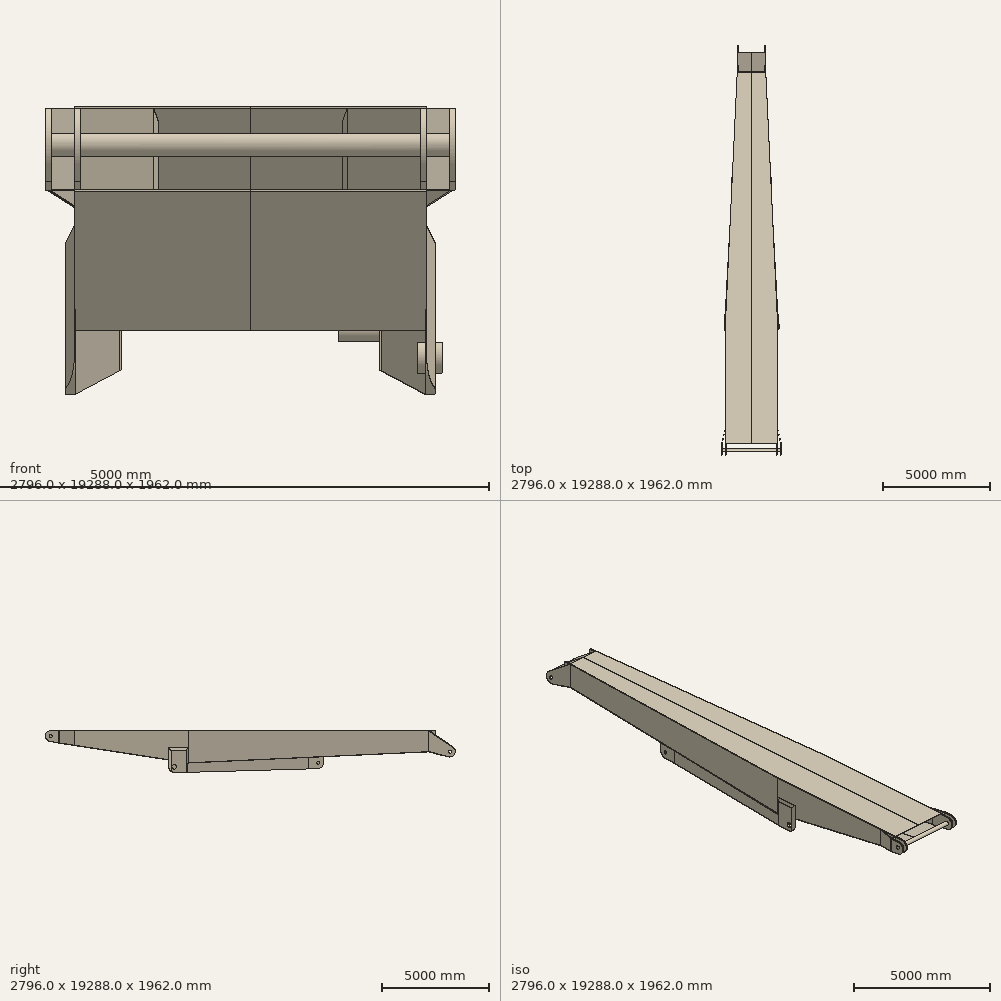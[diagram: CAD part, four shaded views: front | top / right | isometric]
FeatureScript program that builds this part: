
annotation { "Feature Type Name" : "Feature", "Feature Type Description" : "" }
export const myFeature = defineFeature(function(context is Context, id is Id, definition is map)
    precondition{}
    {
        {
            var Q0;
            Q0=qCreatedBy(makeId("Right.planeOp"),FACE);
            cPlane(context, id + "F0", {"entities" : qUnion([Q0]), "cplaneType" : CPlaneType.OFFSET, "offset" : (2384 / 2) * mm, "width" : 150 * mm, "height" : 150 * mm});
        }
        {
            var Q0;
            Q0=qCreatedBy(id+"F0.planeOp",FACE);
            var sketch = newSketch(context, id + "F1", { "sketchPlane" : qUnion([Q0])});
            skCircle(sketch, "E0", {"center": v(0, 0) * mm, "radius": 250 * mm});
            skLineSegment(sketch, "E1", {"start": v(0, 0) * mm, "end": v(5800, 0) * mm, "construction": true});
            skLineSegment(sketch, "E2", {"start": v(5800, 0) * mm, "end": v(5800, -1450) * mm, "construction": true});
            skCircle(sketch, "E3", {"center": v(5800, -1450) * mm, "radius": 250 * mm});
            skLineSegment(sketch, "E4", {"start": v(0, 250) * mm, "end": v(6480, 250) * mm});
            skLineSegment(sketch, "E5", {"start": v(6480, 250) * mm, "end": v(6480, -1250) * mm});
            skLineSegment(sketch, "E6", {"start": v(6480, -1250) * mm, "end": v(-38.02, -247.1) * mm});
            skLineSegment(sketch, "E7", {"start": v(5550, -1450) * mm, "end": v(5550, -1106.9) * mm});
            skLineSegment(sketch, "E8", {"start": v(6480, -1250) * mm, "end": v(5950.6, -1649.55) * mm});
            skCircle(sketch, "E9", {"center": v(0, 0) * mm, "radius": 80 * mm});
            skCircle(sketch, "E10", {"center": v(5800, -1450) * mm, "radius": 105 * mm});
            skLineSegment(sketch, "E11", {"start": v(5550, -1106.9) * mm, "end": v(5550, -550) * mm});
            skLineSegment(sketch, "E12", {"start": v(5550, -550) * mm, "end": v(6480, -550) * mm});
            skLineSegment(sketch, "E13", {"start": v(1050, -414.5) * mm, "end": v(1050, 250) * mm});
            skLineSegment(sketch, "E14", {"start": v(750, -368.34) * mm, "end": v(750, 250) * mm});
            skLineSegment(sketch, "E15", {"start": v(352, -307.1) * mm, "end": v(352, 250) * mm});
            skLineSegment(sketch, "E16", {"start": v(3750, 250) * mm, "end": v(3750, -829.94) * mm});
            skLineSegment(sketch, "E17", {"start": v(5520, 250) * mm, "end": v(5520, -1102.29) * mm});
            skLineSegment(sketch, "E18", {"start": v(6450, 250) * mm, "end": v(6450, -2449.1) * mm});
            skLineSegment(sketch, "E19.1.0.0", {"start": v(9277, 250) * mm, "end": v(9277, -2449.1) * mm});
            skLineSegment(sketch, "E19.2.0.0", {"start": v(12104, 250) * mm, "end": v(12104, -2449.1) * mm});
            skLineSegment(sketch, "E19.direction1", {"start": v(9277, -2449.1) * mm, "end": v(6450, -2449.1) * mm, "construction": true});
            skLineSegment(sketch, "E20.0.3.0", {"start": v(14931, 250) * mm, "end": v(14931, -2449.1) * mm});
            skLineSegment(sketch, "E20.0.4.0", {"start": v(17758, 250) * mm, "end": v(17758, -2449.1) * mm});
            skLineSegment(sketch, "E21", {"start": v(6480, -1250) * mm, "end": v(6480, -2099.61) * mm});
            skLineSegment(sketch, "E22", {"start": v(5800, -1700) * mm, "end": v(6480, -1700) * mm});
            skSolve(sketch);
        }
        {
            var Q0;
            Q0=makeQuery(id+"F9OwMfTJPvjxnqe_1.opExtrude","CAP_FACE",FACE,{"disambiguationData":[OSD([sQuery(id+"F1.wireOp",EDGE,"E0"),sQuery(id+"F1.wireOp",EDGE,"E9")])],"isStart":false});
            var Q1;
            {var subQ5=sQuery(id+"F1.wireOp",EDGE,"E15");Q1=makeQuery(id+"F1.imprint","IMPRINT",FACE,{"disambiguationData":[TD([[makeQuery(id+"F1.imprint","IMPRINT",EDGE,{"derivedFrom":subQ5}),1.0]])]});}
            var Q2;
            Q2=makeQuery(id+"F1.imprint","IMPRINT",FACE,{"disambiguationData":[TD([[makeQuery(id+"F1.imprint","IMPRINT",EDGE,{"derivedFrom":sQuery(id+"F1.wireOp",EDGE,"E9")}),-1.0]])]});
            extrude(context, id + "F2", {"entities" : qUnion([Q0, Q1, Q2]), "depth" : 40 * mm});
        }
        {
            var Q0;
            Q0=makeQuery(id+"F2.opExtrude","SWEPT_BODY",BODY,{"disambiguationData":[OSD([sQuery(id+"F1.wireOp",EDGE,"E0"),sQuery(id+"F1.wireOp",EDGE,"E4"),sQuery(id+"F1.wireOp",EDGE,"E6"),sQuery(id+"F1.wireOp",EDGE,"E9"),sQuery(id+"F1.wireOp",EDGE,"E14")])]});
            var Q1;
            Q1=qCreatedBy(makeId("Right.planeOp"),FACE);
            transform(context, id + "F3", {"entities" : qUnion([Q0]), "transformType" : TransformType.TRANSLATION_DISTANCE, "transformDirection" : qUnion([Q1]), "distance" : (176 - 10) * mm, "makeCopy" : false});
        }
        {
            var Q0;
            {var subQ0=sQuery(id+"F1.wireOp",EDGE,"E7");Q0=makeQuery(id+"F1.imprint","IMPRINT",FACE,{"disambiguationData":[TD([[makeQuery(id+"F1.imprint","IMPRINT",EDGE,{"derivedFrom":subQ0}),-1.0]])]});}
            var Q1;
            Q1=makeQuery(id+"F1.imprint","IMPRINT",FACE,{"disambiguationData":[TD([[makeQuery(id+"F1.imprint","IMPRINT",EDGE,{"derivedFrom":sQuery(id+"F1.wireOp",EDGE,"E10")}),-1.0]])]});
            var Q2;
            {var subQ4=sQuery(id+"F1.wireOp",EDGE,"E11");Q2=makeQuery(id+"F1.imprint","IMPRINT",FACE,{"disambiguationData":[TD([[makeQuery(id+"F1.imprint","IMPRINT",EDGE,{"derivedFrom":subQ4}),-1.0]])]});}
            var Q3;
            {var subQ1=sQuery(id+"F1.wireOp",EDGE,"E5");var subQ3=sQuery(id+"F1.wireOp",EDGE,"E12");var subQ4=makeQuery(id+"F1.imprint","INTERSECT",VERTEX,{"derivedFrom":[subQ1,subQ3]});Q3=makeQuery(id+"F1.imprint","IMPRINT",FACE,{"disambiguationData":[TD([[makeQuery(id+"F1.imprint","IMPRINT",EDGE,{"disambiguationData":[TD([[subQ4,1.0]])],"derivedFrom":subQ3}),-1.0]])]});}
            var Q4;
            {var subQ0=sQuery(id+"F1.wireOp",EDGE,"E8");var subQ3=sQuery(id+"F1.wireOp",EDGE,"E18");var subQ5=makeQuery(id+"F1.imprint","INTERSECT",VERTEX,{"derivedFrom":[subQ0,subQ3]});Q4=makeQuery(id+"F1.imprint","IMPRINT",FACE,{"disambiguationData":[TD([[makeQuery(id+"F1.imprint","IMPRINT",EDGE,{"disambiguationData":[TD([[subQ5,1.0]])],"derivedFrom":subQ3}),1.0]])]});}
            var Q5;
            {var subQ0=sQuery(id+"F1.wireOp",EDGE,"E8");var subQ1=sQuery(id+"F1.wireOp",EDGE,"E3");var subQ2=makeQuery(id+"F1.imprint","INTERSECT",VERTEX,{"derivedFrom":[subQ1,subQ0]});Q5=makeQuery(id+"F1.imprint","IMPRINT",FACE,{"disambiguationData":[TD([[makeQuery(id+"F1.imprint","IMPRINT",EDGE,{"disambiguationData":[TD([[subQ2,1.0]])],"derivedFrom":subQ1}),-1.0]])]});}
            var Q6;
            {var subQ3=sQuery(id+"F1.wireOp",EDGE,"E18");var subQ5=sQuery(id+"F1.wireOp",EDGE,"E22");var subQ7=makeQuery(id+"F1.imprint","INTERSECT",VERTEX,{"derivedFrom":[subQ3,subQ5]});Q6=makeQuery(id+"F1.imprint","IMPRINT",FACE,{"disambiguationData":[TD([[makeQuery(id+"F1.imprint","IMPRINT",EDGE,{"disambiguationData":[TD([[subQ7,1.0]])],"derivedFrom":subQ3}),1.0]])]});}
            extrude(context, id + "F4", {"entities" : qUnion([Q0, Q1, Q2, Q3, Q4, Q5, Q6]), "depth" : 70 * mm});
        }
        {
            var Q0;
            Q0=makeQuery(id+"F4.opExtrude","CAP_EDGE",EDGE,{"disambiguationData":[OSD([sQuery(id+"F1.wireOp",EDGE,"E7"),sQuery(id+"F1.wireOp",EDGE,"E11")])],"isStart":false});
            var Q1;
            Q1=makeQuery(id+"F4.opExtrude","CAP_EDGE",EDGE,{"disambiguationData":[OSD([sQuery(id+"F1.wireOp",EDGE,"E5")])],"isStart":false});
            var Q2;
            Q2=makeQuery(id+"F4.opExtrude","CAP_EDGE",EDGE,{"disambiguationData":[OSD([sQuery(id+"F1.wireOp",EDGE,"E12")])],"isStart":false});
            chamfer(context, id + "F5", {"entities" : qUnion([Q0, Q1, Q2]), "chamferType" : ChamferType.TWO_OFFSETS, "width1" : 60 * mm, "oppositeDirection" : false, "width2" : 120 * mm});
        }
        {
            var Q0;
            {var subQ0=sQuery(id+"F1.wireOp",EDGE,"E11");Q0=makeQuery(id+"F1.imprint","IMPRINT",FACE,{"disambiguationData":[TD([[makeQuery(id+"F1.imprint","IMPRINT",EDGE,{"derivedFrom":subQ0}),1.0]])]});}
            var Q1;
            {var subQ0=sQuery(id+"F1.wireOp",EDGE,"E13");Q1=makeQuery(id+"F1.imprint","IMPRINT",FACE,{"disambiguationData":[TD([[makeQuery(id+"F1.imprint","IMPRINT",EDGE,{"derivedFrom":subQ0}),1.0]])]});}
            var Q2;
            {var subQ0=sQuery(id+"F1.wireOp",EDGE,"E16");Q2=makeQuery(id+"F1.imprint","IMPRINT",FACE,{"disambiguationData":[TD([[makeQuery(id+"F1.imprint","IMPRINT",EDGE,{"derivedFrom":subQ0}),1.0]])]});}
            var Q3;
            {var subQ0=sQuery(id+"F1.wireOp",EDGE,"E13");Q3=makeQuery(id+"F1.imprint","IMPRINT",FACE,{"disambiguationData":[TD([[makeQuery(id+"F1.imprint","IMPRINT",EDGE,{"derivedFrom":subQ0}),-1.0]])]});}
            var Q4;
            {var subQ0=sQuery(id+"F1.wireOp",EDGE,"E5");var subQ1=sQuery(id+"F1.wireOp",EDGE,"E4");var subQ2=makeQuery(id+"F1.imprint","INTERSECT",VERTEX,{"derivedFrom":[subQ1,subQ0]});Q4=makeQuery(id+"F1.imprint","IMPRINT",FACE,{"disambiguationData":[TD([[makeQuery(id+"F1.imprint","IMPRINT",EDGE,{"disambiguationData":[TD([[subQ2,1.0]])],"derivedFrom":subQ1}),-1.0]])]});}
            extrude(context, id + "F6", {"entities" : qUnion([Q0, Q1, Q2, Q3, Q4]), "depth" : 10 * mm});
        }
        {
            var Q0;
            Q0=makeQuery(id+"F1.imprint","IMPRINT",FACE,{"disambiguationData":[TD([[makeQuery(id+"F1.imprint","IMPRINT",EDGE,{"derivedFrom":sQuery(id+"F1.wireOp",EDGE,"E9")}),-1.0]])]});
            var Q1;
            {var subQ5=sQuery(id+"F1.wireOp",EDGE,"E14");Q1=makeQuery(id+"F1.imprint","IMPRINT",FACE,{"disambiguationData":[TD([[makeQuery(id+"F1.imprint","IMPRINT",EDGE,{"derivedFrom":subQ5}),1.0]])]});}
            var Q2;
            {var subQ5=sQuery(id+"F1.wireOp",EDGE,"E15");Q2=makeQuery(id+"F1.imprint","IMPRINT",FACE,{"disambiguationData":[TD([[makeQuery(id+"F1.imprint","IMPRINT",EDGE,{"derivedFrom":subQ5}),1.0]])]});}
            extrude(context, id + "F7", {"entities" : qUnion([Q0, Q1, Q2]), "oppositeDirection" : true, "depth" : 30 * mm, "hasSecondDirection" : true, "secondDirectionOppositeDirection" : false, "secondDirectionDepth" : 10 * mm});
        }
        {
            var Q0;
            Q0=qCreatedBy(makeId("Top.planeOp"),FACE);
            cPlane(context, id + "F8", {"entities" : qUnion([Q0]), "cplaneType" : CPlaneType.OFFSET, "offset" : 250 * mm, "width" : 150 * mm, "height" : 150 * mm});
        }
        {
            var Q0;
            Q0=qCreatedBy(id+"F8.planeOp",FACE);
            var sketch = newSketch(context, id + "F9", { "sketchPlane" : qUnion([Q0])});
            skLineSegment(sketch, "E23", {"start": v(0, 338) * mm, "end": v(1202, 338) * mm});
            skLineSegment(sketch, "E24", {"start": v(1202, 338) * mm, "end": v(1202, 6480) * mm});
            skLineSegment(sketch, "E25", {"start": v(1202, 6480) * mm, "end": v(0, 6480) * mm});
            skLineSegment(sketch, "E26", {"start": v(0, 6480) * mm, "end": v(0, 338) * mm});
            skLineSegment(sketch, "E27", {"start": v(0, 6480) * mm, "end": v(0, 17788) * mm});
            skLineSegment(sketch, "E28", {"start": v(0, 17788) * mm, "end": v(670.76, 17788) * mm});
            skLineSegment(sketch, "E29", {"start": v(1202, 6480) * mm, "end": v(670.76, 17788) * mm});
            skLineSegment(sketch, "E30", {"start": v(1191.99, 6480) * mm, "end": v(660.75, 17788) * mm});
            skPoint(sketch, "E31.0", {"position": v(0, 0) * mm});
            skSolve(sketch);
        }
        {
            var Q0;
            {var subQ0=sQuery(id+"F9.wireOp",EDGE,"E25");Q0=makeQuery(id+"F9.imprint","IMPRINT",FACE,{"disambiguationData":[TD([[makeQuery(id+"F9.imprint","IMPRINT",EDGE,{"derivedFrom":subQ0}),1.0]])]});}
            var Q1;
            Q1=makeQuery(id+"F9.imprint","IMPRINT",FACE,{"disambiguationData":[TD([[makeQuery(id+"F9.imprint","IMPRINT",EDGE,{"derivedFrom":sQuery(id+"F9.wireOp",EDGE,"E25")}),-1.0]])]});
            extrude(context, id + "F10", {"entities" : qUnion([Q0, Q1]), "depth" : 12 * mm});
        }
        {
            var Q0;
            Q0=makeQuery(id+"F2.opExtrude","SWEPT_FACE",FACE,{"disambiguationData":[OSD([sQuery(id+"F1.wireOp",EDGE,"E4")])]});
            var sketch = newSketch(context, id + "F11", { "sketchPlane" : qUnion([Q0])});
            skLineSegment(sketch, "E32.0", {"start": v(1202, 338) * mm, "end": v(1202, 6480) * mm});
            skLineSegment(sketch, "E33", {"start": v(1358, 352) * mm, "end": v(1358, 402) * mm});
            skLineSegment(sketch, "E34", {"start": v(1358, 402) * mm, "end": v(1202, 1050.5) * mm});
            skLineSegment(sketch, "E35.0", {"start": v(1373.43, 402) * mm, "end": v(1202, 1114.64) * mm});
            skLineSegment(sketch, "E36", {"start": v(1373.43, 402) * mm, "end": v(1398, 352) * mm});
            skLineSegment(sketch, "E37", {"start": v(1398, 352) * mm, "end": v(1358, 352) * mm});
            skLineSegment(sketch, "E38", {"start": v(1202, 1114.64) * mm, "end": v(1202, 1050.5) * mm});
            skLineSegment(sketch, "E39.bottom", {"start": v(1358, 352) * mm, "end": v(1202, 352) * mm});
            skLineSegment(sketch, "E39.top", {"start": v(1358, 340) * mm, "end": v(1202, 340) * mm});
            skLineSegment(sketch, "E39.left", {"start": v(1358, 352) * mm, "end": v(1358, 340) * mm});
            skLineSegment(sketch, "E39.right", {"start": v(1202, 352) * mm, "end": v(1202, 340) * mm});
            skSolve(sketch);
        }
        {
            var Q0;
            Q0=makeQuery(id+"F11.imprint","IMPRINT",FACE,{"disambiguationData":[TD([[makeQuery(id+"F11.imprint","IMPRINT",EDGE,{"derivedFrom":sQuery(id+"F11.wireOp",EDGE,"E33")}),-1.0]])]});
            extrude(context, id + "F12", {"entities" : qUnion([Q0]), "oppositeDirection" : true, "depth" : 800 * mm});
        }
        {
            var Q0;
            Q0=makeQuery(id+"F11.imprint","IMPRINT",FACE,{"disambiguationData":[TD([[makeQuery(id+"F11.imprint","IMPRINT",EDGE,{"derivedFrom":sQuery(id+"F11.wireOp",EDGE,"E39.bottom")}),1.0]])]});
            extrude(context, id + "F13", {"entities" : qUnion([Q0]), "oppositeDirection" : true, "depth" : 1000 * mm});
        }
        {
            var Q0;
            Q0=makeQuery(id+"F2.opExtrude","SWEPT_FACE",FACE,{"disambiguationData":[OSD([sQuery(id+"F1.wireOp",EDGE,"E6")])]});
            var sketch = newSketch(context, id + "F14", { "sketchPlane" : qUnion([Q0])});
            skLineSegment(sketch, "E40.bottom", {"start": v(1398, -318.7) * mm, "end": v(966.19, -318.7) * mm});
            skLineSegment(sketch, "E40.top", {"start": v(1398, -1467.1) * mm, "end": v(966.19, -1467.1) * mm});
            skLineSegment(sketch, "E40.left", {"start": v(1398, -318.7) * mm, "end": v(1398, -1467.1) * mm});
            skLineSegment(sketch, "E40.right", {"start": v(966.19, -318.7) * mm, "end": v(966.19, -1467.1) * mm});
            skSolve(sketch);
        }
        {
            var Q0;
            Q0 = qSketchRegion(id + "F14", true);
            extrude(context, id + "F15", {"entities" : qUnion([Q0]), "operationType" : NewBodyOperationType.REMOVE, "depth" : 500 * mm});
        }
        {
            var Q0;
            {var subQ0=sQuery(id+"F9.wireOp",EDGE,"E29");Q0=makeQuery(id+"F9.imprint","IMPRINT",FACE,{"disambiguationData":[TD([[makeQuery(id+"F9.imprint","IMPRINT",EDGE,{"derivedFrom":subQ0}),1.0]])]});}
            extrude(context, id + "F16", {"entities" : qUnion([Q0]), "oppositeDirection" : true, "depth" : 1500 * mm});
        }
        {
            var Q0;
            Q0=qCreatedBy(makeId("Right.planeOp"),FACE);
            var sketch = newSketch(context, id + "F17", { "sketchPlane" : qUnion([Q0])});
            skLineSegment(sketch, "E41.left", {"start": v(6480, -1250) * mm, "end": v(6480, -1250) * mm});
            skLineSegment(sketch, "E42", {"start": v(6480, -1250) * mm, "end": v(17788, -726.7) * mm});
            skLineSegment(sketch, "E43", {"start": v(17788, -726.7) * mm, "end": v(17837.95, -724.39) * mm});
            skLineSegment(sketch, "E44", {"start": v(17837.95, -724.39) * mm, "end": v(17837.95, -1250) * mm});
            skLineSegment(sketch, "E45", {"start": v(17837.95, -1250) * mm, "end": v(17788, -1250) * mm});
            skLineSegment(sketch, "E46.0", {"start": v(6480, -1250) * mm, "end": v(17788, -1250) * mm});
            skSolve(sketch);
        }
        {
            var Q0;
            {var subQ0=sQuery(id+"F17.wireOp",EDGE,"E42");Q0=makeQuery(id+"F17.imprint","IMPRINT",FACE,{"disambiguationData":[TD([[makeQuery(id+"F17.imprint","IMPRINT",EDGE,{"derivedFrom":subQ0}),-1.0]])]});}
            var Q1;
            {var subQ0=sQuery(id+"F17.wireOp",EDGE,"E43");Q1=makeQuery(id+"F17.imprint","IMPRINT",FACE,{"disambiguationData":[TD([[makeQuery(id+"F17.imprint","IMPRINT",EDGE,{"derivedFrom":subQ0}),-1.0]])]});}
            extrude(context, id + "F18", {"entities" : qUnion([Q0, Q1]), "operationType" : NewBodyOperationType.REMOVE, "endBound" : BoundingType.THROUGH_ALL, "depth" : 25 * mm});
        }
        {
            var Q0;
            Q0=makeQuery(id+"F18.boolean.opBoolean","COPY",FACE,{"derivedFrom":makeQuery(id+"F18.opExtrude","SWEPT_FACE",FACE,{"disambiguationData":[OSD([sQuery(id+"F17.wireOp",EDGE,"E42"),sQuery(id+"F17.wireOp",EDGE,"E43")])]})});
            var sketch = newSketch(context, id + "F19", { "sketchPlane" : qUnion([Q0])});
            skLineSegment(sketch, "E47", {"start": v(1202, -6415.29) * mm, "end": v(670.76, -17735.39) * mm});
            skLineSegment(sketch, "E48", {"start": v(670.76, -17735.39) * mm, "end": v(0, -17735.39) * mm});
            skLineSegment(sketch, "E49", {"start": v(1202, -6415.29) * mm, "end": v(0, -6415.29) * mm});
            skLineSegment(sketch, "E50", {"start": v(0, -6415.29) * mm, "end": v(0, -17735.39) * mm});
            skSolve(sketch);
        }
        {
            var Q0;
            Q0=makeQuery(id+"F19.imprint","IMPRINT",FACE,{"disambiguationData":[TD([[makeQuery(id+"F19.imprint","IMPRINT",EDGE,{"derivedFrom":sQuery(id+"F19.wireOp",EDGE,"E48")}),-1.0]])]});
            var Q1;
            {var subQ0=sQuery(id+"F19.wireOp",EDGE,"E47");Q1=makeQuery(id+"F19.imprint","IMPRINT",FACE,{"disambiguationData":[TD([[makeQuery(id+"F19.imprint","IMPRINT",EDGE,{"derivedFrom":subQ0}),-1.0]])]});}
            var Q2;
            Q2=makeQuery(id+"F19.imprint","IMPRINT",FACE,{"disambiguationData":[TD([[makeQuery(id+"F19.imprint","IMPRINT",EDGE,{"derivedFrom":sQuery(id+"F19.wireOp",EDGE,"E49")}),1.0]])]});
            extrude(context, id + "F20", {"entities" : qUnion([Q0, Q1, Q2]), "depth" : 12 * mm});
        }
        {
            var Q0;
            {var subQ0=sQuery(id+"F1.wireOp",EDGE,"E11");Q0=makeQuery(id+"F1.imprint","IMPRINT",FACE,{"disambiguationData":[TD([[makeQuery(id+"F1.imprint","IMPRINT",EDGE,{"derivedFrom":subQ0}),1.0]])]});}
            var sketch = newSketch(context, id + "F21", { "sketchPlane" : qUnion([Q0])});
            skPoint(sketch, "E51.0", {"position": v(750, -368.34) * mm});
            skLineSegment(sketch, "E52", {"start": v(337.17, -304.82) * mm, "end": v(6480, -1250) * mm});
            skLineSegment(sketch, "E53", {"start": v(6480, -1250) * mm, "end": v(6478.18, -1261.86) * mm});
            skLineSegment(sketch, "E54", {"start": v(6480, -1250) * mm, "end": v(6480.55, -1261.99) * mm});
            skLineSegment(sketch, "E55", {"start": v(6480.55, -1261.99) * mm, "end": v(6478.18, -1261.86) * mm});
            skLineSegment(sketch, "E56", {"start": v(6478.18, -1261.86) * mm, "end": v(335.35, -316.68) * mm});
            skLineSegment(sketch, "E57", {"start": v(335.35, -316.68) * mm, "end": v(337.17, -304.82) * mm});
            skLineSegment(sketch, "E58.0", {"start": v(6480.55, -1261.99) * mm, "end": v(6480, -1250) * mm});
            skSolve(sketch);
        }
        {
            var Q0;
            {var subQ0=sQuery(id+"F21.wireOp",EDGE,"E53");Q0=makeQuery(id+"F21.imprint","IMPRINT",FACE,{"disambiguationData":[TD([[makeQuery(id+"F21.imprint","IMPRINT",EDGE,{"derivedFrom":subQ0}),-1.0]])]});}
            var Q1;
            Q1=makeQuery(id+"F21.imprint","IMPRINT",FACE,{"disambiguationData":[TD([[makeQuery(id+"F21.imprint","IMPRINT",EDGE,{"derivedFrom":sQuery(id+"F21.wireOp",EDGE,"E53")}),1.0]])]});
            var Q2;
            Q2=makeQuery(id+"F10.opExtrude","SWEPT_FACE",FACE,{"disambiguationData":[OSD([sQuery(id+"F9.wireOp",EDGE,"E26"),sQuery(id+"F9.wireOp",EDGE,"E27")])]});
            extrude(context, id + "F22", {"entities" : qUnion([Q0, Q1]), "endBound" : BoundingType.UP_TO_SURFACE, "oppositeDirection" : true, "endBoundEntityFace" : qUnion([Q2]), "depth" : 25 * mm, "hasSecondDirection" : true, "secondDirectionOppositeDirection" : false, "secondDirectionDepth" : 10 * mm});
        }
        {
            var Q0;
            Q0=makeQuery(id+"F4.opExtrude","SWEPT_BODY",BODY,{"disambiguationData":[OSD([sQuery(id+"F1.wireOp",EDGE,"E3"),sQuery(id+"F1.wireOp",EDGE,"E5"),sQuery(id+"F1.wireOp",EDGE,"E7"),sQuery(id+"F1.wireOp",EDGE,"E8"),sQuery(id+"F1.wireOp",EDGE,"E10"),sQuery(id+"F1.wireOp",EDGE,"E11"),sQuery(id+"F1.wireOp",EDGE,"E12")])]});
            var Q1;
            Q1=makeQuery(id+"F22.opExtrude","SWEPT_BODY",BODY,{"disambiguationData":[OSD([sQuery(id+"F21.wireOp",EDGE,"E52"),sQuery(id+"F21.wireOp",EDGE,"E53"),sQuery(id+"F21.wireOp",EDGE,"E56"),sQuery(id+"F21.wireOp",EDGE,"E57")])]});
            booleanBodies(context, id + "F23", {"operationType" : BooleanOperationType.SUBTRACTION, "tools" : qUnion([Q0]), "targets" : qUnion([Q1]), "keepTools" : true});
        }
        {
            var Q0;
            Q0=qCreatedBy(id+"F8.planeOp",FACE);
            var sketch = newSketch(context, id + "F24", { "sketchPlane" : qUnion([Q0])});
            skPoint(sketch, "E59.0", {"position": v(1192, 3750) * mm});
            skPoint(sketch, "E60.0", {"position": v(1192, 352) * mm});
            skPoint(sketch, "E61.0", {"position": v(1192, 1050) * mm});
            skPoint(sketch, "E62.0", {"position": v(1192, 5520) * mm});
            skPoint(sketch, "E63.0", {"position": v(1192, 6450) * mm});
            skPoint(sketch, "E64.0", {"position": v(1192, 9277) * mm});
            skPoint(sketch, "E65.0", {"position": v(1192, 12104) * mm});
            skPoint(sketch, "E66.0", {"position": v(1192, 14931) * mm});
            skPoint(sketch, "E67.0", {"position": v(1192, 17758) * mm});
            skLineSegment(sketch, "E68.bottom", {"start": v(1192, 340) * mm, "end": v(0, 340) * mm});
            skLineSegment(sketch, "E68.top", {"start": v(1192, 352) * mm, "end": v(0, 352) * mm});
            skLineSegment(sketch, "E68.left", {"start": v(1192, 340) * mm, "end": v(1192, 352) * mm});
            skLineSegment(sketch, "E68.right", {"start": v(0, 340) * mm, "end": v(0, 352) * mm});
            skPoint(sketch, "E69.0", {"position": v(0, 0) * mm});
            skLineSegment(sketch, "E70", {"start": v(0, 0) * mm, "end": v(0, 18574) * mm, "construction": true});
            skLineSegment(sketch, "E71.bottom", {"start": v(1192, 1050) * mm, "end": v(0, 1050) * mm});
            skLineSegment(sketch, "E71.top", {"start": v(1192, 1062) * mm, "end": v(0, 1062) * mm});
            skLineSegment(sketch, "E71.left", {"start": v(1192, 1050) * mm, "end": v(1192, 1062) * mm});
            skLineSegment(sketch, "E71.right", {"start": v(0, 1050) * mm, "end": v(0, 1062) * mm});
            skLineSegment(sketch, "E72.bottom", {"start": v(1192, 3750) * mm, "end": v(0, 3750) * mm});
            skLineSegment(sketch, "E72.top", {"start": v(1192, 3762) * mm, "end": v(0, 3762) * mm});
            skLineSegment(sketch, "E72.left", {"start": v(1192, 3750) * mm, "end": v(1192, 3762) * mm});
            skLineSegment(sketch, "E72.right", {"start": v(0, 3750) * mm, "end": v(0, 3762) * mm});
            skLineSegment(sketch, "E73.bottom", {"start": v(1192, 5520) * mm, "end": v(0, 5520) * mm});
            skLineSegment(sketch, "E73.top", {"start": v(1192, 5530) * mm, "end": v(0, 5530) * mm});
            skLineSegment(sketch, "E73.left", {"start": v(1192, 5520) * mm, "end": v(1192, 5530) * mm});
            skLineSegment(sketch, "E73.right", {"start": v(0, 5520) * mm, "end": v(0, 5530) * mm});
            skLineSegment(sketch, "E74.bottom", {"start": v(1192, 6450) * mm, "end": v(0, 6450) * mm});
            skLineSegment(sketch, "E74.top", {"start": v(1192, 6460) * mm, "end": v(0, 6460) * mm});
            skLineSegment(sketch, "E74.left", {"start": v(1192, 6450) * mm, "end": v(1192, 6460) * mm});
            skLineSegment(sketch, "E74.right", {"start": v(0, 6450) * mm, "end": v(0, 6460) * mm});
            skLineSegment(sketch, "E75.bottom", {"start": v(1192, 9277) * mm, "end": v(0, 9277) * mm});
            skLineSegment(sketch, "E75.top", {"start": v(1192, 9287) * mm, "end": v(0, 9287) * mm});
            skLineSegment(sketch, "E75.left", {"start": v(1192, 9277) * mm, "end": v(1192, 9287) * mm});
            skLineSegment(sketch, "E75.right", {"start": v(0, 9277) * mm, "end": v(0, 9287) * mm});
            skLineSegment(sketch, "E76.bottom", {"start": v(1192, 12104) * mm, "end": v(0, 12104) * mm});
            skLineSegment(sketch, "E76.top", {"start": v(1192, 12114) * mm, "end": v(0, 12114) * mm});
            skLineSegment(sketch, "E76.left", {"start": v(1192, 12104) * mm, "end": v(1192, 12114) * mm});
            skLineSegment(sketch, "E76.right", {"start": v(0, 12104) * mm, "end": v(0, 12114) * mm});
            skLineSegment(sketch, "E77.bottom", {"start": v(1192, 14931) * mm, "end": v(0, 14931) * mm});
            skLineSegment(sketch, "E77.top", {"start": v(1192, 14941) * mm, "end": v(0, 14941) * mm});
            skLineSegment(sketch, "E77.left", {"start": v(1192, 14931) * mm, "end": v(1192, 14941) * mm});
            skLineSegment(sketch, "E77.right", {"start": v(0, 14931) * mm, "end": v(0, 14941) * mm});
            skLineSegment(sketch, "E78.bottom", {"start": v(1192, 17758) * mm, "end": v(0, 17758) * mm});
            skLineSegment(sketch, "E78.top", {"start": v(1192, 17768) * mm, "end": v(0, 17768) * mm});
            skLineSegment(sketch, "E78.left", {"start": v(1192, 17758) * mm, "end": v(1192, 17768) * mm});
            skLineSegment(sketch, "E78.right", {"start": v(0, 17758) * mm, "end": v(0, 17768) * mm});
            skSolve(sketch);
        }
        {
            var Q0;
            Q0=makeQuery(id+"F24.imprint","IMPRINT",FACE,{"disambiguationData":[TD([[makeQuery(id+"F24.imprint","IMPRINT",EDGE,{"derivedFrom":sQuery(id+"F24.wireOp",EDGE,"E68.bottom")}),-1.0]])]});
            var Q1;
            Q1=makeQuery(id+"F24.imprint","IMPRINT",FACE,{"disambiguationData":[TD([[makeQuery(id+"F24.imprint","IMPRINT",EDGE,{"derivedFrom":sQuery(id+"F24.wireOp",EDGE,"E71.bottom")}),-1.0]])]});
            var Q2;
            Q2=makeQuery(id+"F24.imprint","IMPRINT",FACE,{"disambiguationData":[TD([[makeQuery(id+"F24.imprint","IMPRINT",EDGE,{"derivedFrom":sQuery(id+"F24.wireOp",EDGE,"E72.bottom")}),-1.0]])]});
            var Q3;
            Q3=makeQuery(id+"F24.imprint","IMPRINT",FACE,{"disambiguationData":[TD([[makeQuery(id+"F24.imprint","IMPRINT",EDGE,{"derivedFrom":sQuery(id+"F24.wireOp",EDGE,"E73.bottom")}),-1.0]])]});
            var Q4;
            Q4=makeQuery(id+"F24.imprint","IMPRINT",FACE,{"disambiguationData":[TD([[makeQuery(id+"F24.imprint","IMPRINT",EDGE,{"derivedFrom":sQuery(id+"F24.wireOp",EDGE,"E74.bottom")}),-1.0]])]});
            var Q5;
            Q5=makeQuery(id+"F24.imprint","IMPRINT",FACE,{"disambiguationData":[TD([[makeQuery(id+"F24.imprint","IMPRINT",EDGE,{"derivedFrom":sQuery(id+"F24.wireOp",EDGE,"E75.bottom")}),-1.0]])]});
            var Q6;
            Q6=makeQuery(id+"F24.imprint","IMPRINT",FACE,{"disambiguationData":[TD([[makeQuery(id+"F24.imprint","IMPRINT",EDGE,{"derivedFrom":sQuery(id+"F24.wireOp",EDGE,"E76.bottom")}),-1.0]])]});
            var Q7;
            Q7=makeQuery(id+"F24.imprint","IMPRINT",FACE,{"disambiguationData":[TD([[makeQuery(id+"F24.imprint","IMPRINT",EDGE,{"derivedFrom":sQuery(id+"F24.wireOp",EDGE,"E77.bottom")}),-1.0]])]});
            var Q8;
            Q8=makeQuery(id+"F24.imprint","IMPRINT",FACE,{"disambiguationData":[TD([[makeQuery(id+"F24.imprint","IMPRINT",EDGE,{"derivedFrom":sQuery(id+"F24.wireOp",EDGE,"E78.bottom")}),-1.0]])]});
            extrude(context, id + "F25", {"entities" : qUnion([Q0, Q1, Q2, Q3, Q4, Q5, Q6, Q7, Q8]), "oppositeDirection" : true, "depth" : 2000 * mm});
        }
        {
            var Q0;
            Q0=makeQuery(id+"F22.opExtrude","SWEPT_BODY",BODY,{"disambiguationData":[OSD([sQuery(id+"F21.wireOp",EDGE,"E52"),sQuery(id+"F21.wireOp",EDGE,"E54"),sQuery(id+"F21.wireOp",EDGE,"E55"),sQuery(id+"F21.wireOp",EDGE,"E56"),sQuery(id+"F21.wireOp",EDGE,"E57")])]});
            var Q1;
            Q1=makeQuery(id+"F20.opExtrude","SWEPT_BODY",BODY,{"disambiguationData":[OSD([sQuery(id+"F19.wireOp",EDGE,"E47"),sQuery(id+"F19.wireOp",EDGE,"E48"),sQuery(id+"F19.wireOp",EDGE,"E49"),sQuery(id+"F19.wireOp",EDGE,"E50")])]});
            var Q2;
            Q2=makeQuery(id+"F16.opExtrude","SWEPT_BODY",BODY,{"disambiguationData":[OSD([sQuery(id+"F9.wireOp",EDGE,"E25"),sQuery(id+"F9.wireOp",EDGE,"E28"),sQuery(id+"F9.wireOp",EDGE,"E29"),sQuery(id+"F9.wireOp",EDGE,"E30")])]});
            var Q3;
            Q3=makeQuery(id+"F7.opExtrude","SWEPT_BODY",BODY,{"disambiguationData":[OSD([sQuery(id+"F1.wireOp",EDGE,"E0"),sQuery(id+"F1.wireOp",EDGE,"E4"),sQuery(id+"F1.wireOp",EDGE,"E6"),sQuery(id+"F1.wireOp",EDGE,"E9"),sQuery(id+"F1.wireOp",EDGE,"E14")])]});
            var Q4;
            Q4=makeQuery(id+"F6.opExtrude","SWEPT_BODY",BODY,{"disambiguationData":[OSD([sQuery(id+"F1.wireOp",EDGE,"E4"),sQuery(id+"F1.wireOp",EDGE,"E5"),sQuery(id+"F1.wireOp",EDGE,"E6"),sQuery(id+"F1.wireOp",EDGE,"E11"),sQuery(id+"F1.wireOp",EDGE,"E12"),sQuery(id+"F1.wireOp",EDGE,"E14")])]});
            var Q5;
            Q5=makeQuery(id+"F4.opExtrude","SWEPT_BODY",BODY,{"disambiguationData":[OSD([sQuery(id+"F1.wireOp",EDGE,"E3"),sQuery(id+"F1.wireOp",EDGE,"E5"),sQuery(id+"F1.wireOp",EDGE,"E7"),sQuery(id+"F1.wireOp",EDGE,"E8"),sQuery(id+"F1.wireOp",EDGE,"E10"),sQuery(id+"F1.wireOp",EDGE,"E11"),sQuery(id+"F1.wireOp",EDGE,"E12")])]});
            var Q6;
            Q6=makeQuery(id+"F25.opExtrude","SWEPT_BODY",BODY,{"disambiguationData":[OSD([sQuery(id+"F24.wireOp",EDGE,"E68.bottom"),sQuery(id+"F24.wireOp",EDGE,"E68.top"),sQuery(id+"F24.wireOp",EDGE,"E68.left"),sQuery(id+"F24.wireOp",EDGE,"E68.right")])]});
            var Q7;
            Q7=makeQuery(id+"F25.opExtrude","SWEPT_BODY",BODY,{"disambiguationData":[OSD([sQuery(id+"F24.wireOp",EDGE,"E71.bottom"),sQuery(id+"F24.wireOp",EDGE,"E71.top"),sQuery(id+"F24.wireOp",EDGE,"E71.left"),sQuery(id+"F24.wireOp",EDGE,"E71.right")])]});
            var Q8;
            Q8=makeQuery(id+"F25.opExtrude","SWEPT_BODY",BODY,{"disambiguationData":[OSD([sQuery(id+"F24.wireOp",EDGE,"E72.bottom"),sQuery(id+"F24.wireOp",EDGE,"E72.top"),sQuery(id+"F24.wireOp",EDGE,"E72.left"),sQuery(id+"F24.wireOp",EDGE,"E72.right")])]});
            var Q9;
            Q9=makeQuery(id+"F25.opExtrude","SWEPT_BODY",BODY,{"disambiguationData":[OSD([sQuery(id+"F24.wireOp",EDGE,"E73.bottom"),sQuery(id+"F24.wireOp",EDGE,"E73.top"),sQuery(id+"F24.wireOp",EDGE,"E73.left"),sQuery(id+"F24.wireOp",EDGE,"E73.right")])]});
            var Q10;
            Q10=makeQuery(id+"F25.opExtrude","SWEPT_BODY",BODY,{"disambiguationData":[OSD([sQuery(id+"F24.wireOp",EDGE,"E74.bottom"),sQuery(id+"F24.wireOp",EDGE,"E74.top"),sQuery(id+"F24.wireOp",EDGE,"E74.left"),sQuery(id+"F24.wireOp",EDGE,"E74.right")])]});
            var Q11;
            Q11=makeQuery(id+"F25.opExtrude","SWEPT_BODY",BODY,{"disambiguationData":[OSD([sQuery(id+"F24.wireOp",EDGE,"E75.bottom"),sQuery(id+"F24.wireOp",EDGE,"E75.top"),sQuery(id+"F24.wireOp",EDGE,"E75.left"),sQuery(id+"F24.wireOp",EDGE,"E75.right")])]});
            var Q12;
            Q12=makeQuery(id+"F25.opExtrude","SWEPT_BODY",BODY,{"disambiguationData":[OSD([sQuery(id+"F24.wireOp",EDGE,"E76.bottom"),sQuery(id+"F24.wireOp",EDGE,"E76.top"),sQuery(id+"F24.wireOp",EDGE,"E76.left"),sQuery(id+"F24.wireOp",EDGE,"E76.right")])]});
            var Q13;
            Q13=makeQuery(id+"F25.opExtrude","SWEPT_BODY",BODY,{"disambiguationData":[OSD([sQuery(id+"F24.wireOp",EDGE,"E77.bottom"),sQuery(id+"F24.wireOp",EDGE,"E77.top"),sQuery(id+"F24.wireOp",EDGE,"E77.left"),sQuery(id+"F24.wireOp",EDGE,"E77.right")])]});
            var Q14;
            Q14=makeQuery(id+"F25.opExtrude","SWEPT_BODY",BODY,{"disambiguationData":[OSD([sQuery(id+"F24.wireOp",EDGE,"E78.bottom"),sQuery(id+"F24.wireOp",EDGE,"E78.top"),sQuery(id+"F24.wireOp",EDGE,"E78.left"),sQuery(id+"F24.wireOp",EDGE,"E78.right")])]});
            booleanBodies(context, id + "F26", {"operationType" : BooleanOperationType.SUBTRACTION, "tools" : qUnion([Q0, Q1, Q2, Q3, Q4, Q5]), "targets" : qUnion([Q6, Q7, Q8, Q9, Q10, Q11, Q12, Q13, Q14]), "keepTools" : true});
        }
        {
            var Q0;
            Q0=makeQuery(id+"F26.opBoolean","SPLIT",BODY,{"disambiguationData":[OD(1.0)],"derivedFrom":makeQuery(id+"F25.opExtrude","SWEPT_BODY",BODY,{"disambiguationData":[OSD([sQuery(id+"F24.wireOp",EDGE,"E78.bottom"),sQuery(id+"F24.wireOp",EDGE,"E78.top"),sQuery(id+"F24.wireOp",EDGE,"E78.left"),sQuery(id+"F24.wireOp",EDGE,"E78.right")])]})});
            var Q1;
            Q1=makeQuery(id+"F26.opBoolean","SPLIT",BODY,{"disambiguationData":[OD(1.0)],"derivedFrom":makeQuery(id+"F25.opExtrude","SWEPT_BODY",BODY,{"disambiguationData":[OSD([sQuery(id+"F24.wireOp",EDGE,"E77.bottom"),sQuery(id+"F24.wireOp",EDGE,"E77.top"),sQuery(id+"F24.wireOp",EDGE,"E77.left"),sQuery(id+"F24.wireOp",EDGE,"E77.right")])]})});
            var Q2;
            Q2=makeQuery(id+"F26.opBoolean","SPLIT",BODY,{"disambiguationData":[OD(1.0)],"derivedFrom":makeQuery(id+"F25.opExtrude","SWEPT_BODY",BODY,{"disambiguationData":[OSD([sQuery(id+"F24.wireOp",EDGE,"E76.bottom"),sQuery(id+"F24.wireOp",EDGE,"E76.top"),sQuery(id+"F24.wireOp",EDGE,"E76.left"),sQuery(id+"F24.wireOp",EDGE,"E76.right")])]})});
            var Q3;
            Q3=makeQuery(id+"F26.opBoolean","SPLIT",BODY,{"disambiguationData":[OD(1.0)],"derivedFrom":makeQuery(id+"F25.opExtrude","SWEPT_BODY",BODY,{"disambiguationData":[OSD([sQuery(id+"F24.wireOp",EDGE,"E75.bottom"),sQuery(id+"F24.wireOp",EDGE,"E75.top"),sQuery(id+"F24.wireOp",EDGE,"E75.left"),sQuery(id+"F24.wireOp",EDGE,"E75.right")])]})});
            var Q4;
            Q4=makeQuery(id+"F26.opBoolean","SPLIT",BODY,{"disambiguationData":[OD(1.0)],"derivedFrom":makeQuery(id+"F25.opExtrude","SWEPT_BODY",BODY,{"disambiguationData":[OSD([sQuery(id+"F24.wireOp",EDGE,"E74.bottom"),sQuery(id+"F24.wireOp",EDGE,"E74.top"),sQuery(id+"F24.wireOp",EDGE,"E74.left"),sQuery(id+"F24.wireOp",EDGE,"E74.right")])]})});
            var Q5;
            Q5=makeQuery(id+"F26.opBoolean","SPLIT",BODY,{"disambiguationData":[OD(1.0)],"derivedFrom":makeQuery(id+"F25.opExtrude","SWEPT_BODY",BODY,{"disambiguationData":[OSD([sQuery(id+"F24.wireOp",EDGE,"E73.bottom"),sQuery(id+"F24.wireOp",EDGE,"E73.top"),sQuery(id+"F24.wireOp",EDGE,"E73.left"),sQuery(id+"F24.wireOp",EDGE,"E73.right")])]})});
            var Q6;
            Q6=makeQuery(id+"F26.opBoolean","SPLIT",BODY,{"disambiguationData":[OD(1.0)],"derivedFrom":makeQuery(id+"F25.opExtrude","SWEPT_BODY",BODY,{"disambiguationData":[OSD([sQuery(id+"F24.wireOp",EDGE,"E72.bottom"),sQuery(id+"F24.wireOp",EDGE,"E72.top"),sQuery(id+"F24.wireOp",EDGE,"E72.left"),sQuery(id+"F24.wireOp",EDGE,"E72.right")])]})});
            var Q7;
            Q7=makeQuery(id+"F26.opBoolean","SPLIT",BODY,{"disambiguationData":[OD(1.0)],"derivedFrom":makeQuery(id+"F25.opExtrude","SWEPT_BODY",BODY,{"disambiguationData":[OSD([sQuery(id+"F24.wireOp",EDGE,"E71.bottom"),sQuery(id+"F24.wireOp",EDGE,"E71.top"),sQuery(id+"F24.wireOp",EDGE,"E71.left"),sQuery(id+"F24.wireOp",EDGE,"E71.right")])]})});
            var Q8;
            Q8=makeQuery(id+"F26.opBoolean","SPLIT",BODY,{"disambiguationData":[OD(0.0)],"derivedFrom":makeQuery(id+"F25.opExtrude","SWEPT_BODY",BODY,{"disambiguationData":[OSD([sQuery(id+"F24.wireOp",EDGE,"E68.bottom"),sQuery(id+"F24.wireOp",EDGE,"E68.top"),sQuery(id+"F24.wireOp",EDGE,"E68.left"),sQuery(id+"F24.wireOp",EDGE,"E68.right")])]})});
            deleteBodies(context, id + "F27", {"entities" : qUnion([Q0, Q1, Q2, Q3, Q4, Q5, Q6, Q7, Q8])});
        }
        {
            var Q0;
            Q0=qCreatedBy(makeId("Right.planeOp"),FACE);
            cPlane(context, id + "F28", {"entities" : qUnion([Q0]), "cplaneType" : CPlaneType.OFFSET, "offset" : (1321.5 / 2) * mm, "width" : 150 * mm, "height" : 150 * mm});
        }
        {
            var Q0;
            Q0=qCreatedBy(id+"F28.planeOp",FACE);
            var sketch = newSketch(context, id + "F29", { "sketchPlane" : qUnion([Q0])});
            skCircle(sketch, "E79", {"center": v(18788, -730) * mm, "radius": 80 * mm});
            skCircle(sketch, "E80", {"center": v(18788, -730) * mm, "radius": 250 * mm});
            skPoint(sketch, "E81.0", {"position": v(0, 0) * mm});
            skLineSegment(sketch, "E82.0", {"start": v(17788, -726.7) * mm, "end": v(17788, 250) * mm});
            skLineSegment(sketch, "E83", {"start": v(17788, 250) * mm, "end": v(18928.29, -523.07) * mm});
            skLineSegment(sketch, "E84", {"start": v(17788, -726.7) * mm, "end": v(18724.7, -971.85) * mm});
            skLineSegment(sketch, "E85.0", {"start": v(17794.73, 259.93) * mm, "end": v(18728.1, -372.85) * mm});
            skLineSegment(sketch, "E86", {"start": v(17794.73, 259.93) * mm, "end": v(17788, 250) * mm});
            skLineSegment(sketch, "E87", {"start": v(18728.1, -372.85) * mm, "end": v(18721.36, -382.78) * mm});
            skLineSegment(sketch, "E88.0", {"start": v(17788, 262) * mm, "end": v(17788, 250) * mm});
            skLineSegment(sketch, "E89", {"start": v(17788, 262) * mm, "end": v(17794.73, 259.93) * mm});
            skLineSegment(sketch, "E90.0", {"start": v(17790.53, -739.77) * mm, "end": v(18479.8, -920.16) * mm});
            skLineSegment(sketch, "E91", {"start": v(18479.8, -920.16) * mm, "end": v(18482.85, -908.56) * mm});
            skLineSegment(sketch, "E92.0.1", {"start": v(17788, -726.7) * mm, "end": v(17788.55, -738.69) * mm});
            skLineSegment(sketch, "E92.0.3", {"start": v(17788.55, -738.69) * mm, "end": v(17788, -726.7) * mm});
            skLineSegment(sketch, "E93", {"start": v(17788.55, -738.69) * mm, "end": v(17790.53, -739.77) * mm});
            skCircle(sketch, "E94", {"center": v(18058, 200) * mm, "radius": 50 * mm});
            skLineSegment(sketch, "E95", {"start": v(18058, 250) * mm, "end": v(17809.38, 250) * mm});
            skLineSegment(sketch, "E96", {"start": v(18108, 200) * mm, "end": v(18108, 47.55) * mm});
            skSolve(sketch);
        }
        {
            var Q0;
            Q0=makeQuery(id+"F29.imprint","IMPRINT",FACE,{"disambiguationData":[TD([[makeQuery(id+"F29.imprint","IMPRINT",EDGE,{"derivedFrom":sQuery(id+"F29.wireOp",EDGE,"E82.0")}),-1.0]])]});
            var Q1;
            Q1=makeQuery(id+"F29.imprint","IMPRINT",FACE,{"disambiguationData":[TD([[makeQuery(id+"F29.imprint","IMPRINT",EDGE,{"derivedFrom":sQuery(id+"F29.wireOp",EDGE,"E79")}),-1.0]])]});
            var Q2;
            {var subQ3=sQuery(id+"F29.wireOp",EDGE,"E87");Q2=makeQuery(id+"F29.imprint","IMPRINT",FACE,{"disambiguationData":[TD([[makeQuery(id+"F29.imprint","IMPRINT",EDGE,{"derivedFrom":subQ3}),1.0]])]});}
            var Q3;
            {var subQ0=sQuery(id+"F29.wireOp",EDGE,"E94");var subQ1=makeQuery(id+"F29.imprint","INTERSECT",VERTEX,{"derivedFrom":[subQ0,sQuery(id+"F29.wireOp",EDGE,"E95")]});Q3=makeQuery(id+"F29.imprint","IMPRINT",FACE,{"disambiguationData":[TD([[makeQuery(id+"F29.imprint","IMPRINT",EDGE,{"disambiguationData":[TD([[subQ1,1.0]])],"derivedFrom":subQ0}),1.0]])]});}
            var Q4;
            {var subQ0=sQuery(id+"F29.wireOp",EDGE,"E95");Q4=makeQuery(id+"F29.imprint","IMPRINT",FACE,{"disambiguationData":[TD([[makeQuery(id+"F29.imprint","IMPRINT",EDGE,{"derivedFrom":subQ0}),1.0]])]});}
            extrude(context, id + "F30", {"entities" : qUnion([Q0, Q1, Q2, Q3, Q4]), "depth" : 10 * mm, "hasSecondDirection" : true, "secondDirectionOppositeDirection" : true, "secondDirectionDepth" : 30 * mm});
        }
        {
            var Q0;
            Q0=makeQuery(id+"F30.opExtrude","CAP_EDGE",EDGE,{"disambiguationData":[OSD([sQuery(id+"F29.wireOp",EDGE,"E82.0")])],"isStart":true});
            chamfer(context, id + "F31", {"entities" : qUnion([Q0]), "chamferType" : ChamferType.TWO_OFFSETS, "width1" : 30 * mm, "oppositeDirection" : true, "width2" : (4 * 30) * mm, "tangentPropagation" : true});
        }
        {
            var Q0;
            Q0=makeQuery(id+"F29.imprint","IMPRINT",FACE,{"disambiguationData":[TD([[makeQuery(id+"F29.imprint","IMPRINT",EDGE,{"derivedFrom":sQuery(id+"F29.wireOp",EDGE,"E85.0")}),-1.0]])]});
            var Q1;
            Q1=makeQuery(id+"F29.imprint","IMPRINT",FACE,{"disambiguationData":[TD([[makeQuery(id+"F29.imprint","IMPRINT",EDGE,{"derivedFrom":sQuery(id+"F29.wireOp",EDGE,"E86")}),-1.0]])]});
            var Q2;
            Q2=makeQuery(id+"F29.imprint","IMPRINT",FACE,{"disambiguationData":[TD([[makeQuery(id+"F29.imprint","IMPRINT",EDGE,{"derivedFrom":sQuery(id+"F29.wireOp",EDGE,"E90.0")}),1.0]])]});
            var Q3;
            Q3=makeQuery(id+"F30.opExtrude","CAP_FACE",FACE,{"disambiguationData":[OSD([sQuery(id+"F29.wireOp",EDGE,"E79"),sQuery(id+"F29.wireOp",EDGE,"E80"),sQuery(id+"F29.wireOp",EDGE,"E82.0"),sQuery(id+"F29.wireOp",EDGE,"E83"),sQuery(id+"F29.wireOp",EDGE,"E84")])],"isStart":false});
            var Q4;
            Q4=qCreatedBy(makeId("Right.planeOp"),FACE);
            extrude(context, id + "F32", {"entities" : qUnion([Q0, Q1, Q2]), "endBound" : BoundingType.UP_TO_SURFACE, "endBoundEntityFace" : qUnion([Q3]), "depth" : 10 * mm, "hasSecondDirection" : true, "secondDirectionBound" : SecondDirectionBoundingType.UP_TO_SURFACE, "secondDirectionOppositeDirection" : true, "secondDirectionBoundEntityFace" : qUnion([Q4]), "secondDirectionDepth" : 25 * mm});
        }
        {
            var Q0;
            Q0=qCreatedBy(makeId("Right.planeOp"),FACE);
            cPlane(context, id + "F33", {"entities" : qUnion([Q0]), "cplaneType" : CPlaneType.OFFSET, "offset" : 760 * mm + 150 * mm, "width" : 150 * mm, "height" : 150 * mm});
        }
        {
            var Q0;
            Q0=qCreatedBy(id+"F33.planeOp",FACE);
            var sketch = newSketch(context, id + "F34", { "sketchPlane" : qUnion([Q0])});
            skCircle(sketch, "E97", {"center": v(12588, -1267) * mm, "radius": 70 * mm});
            skCircle(sketch, "E98", {"center": v(12588, -1267) * mm, "radius": 250 * mm});
            skPoint(sketch, "E99.0", {"position": v(0, 0) * mm});
            skLineSegment(sketch, "E100.0", {"start": v(12824.45, -968.41) * mm, "end": v(12104, -1001.75) * mm});
            skLineSegment(sketch, "E101", {"start": v(12588, -1267) * mm, "end": v(12837.73, -1255.44) * mm});
            skLineSegment(sketch, "E102", {"start": v(12837.73, -1255.44) * mm, "end": v(12824.45, -968.41) * mm});
            skLineSegment(sketch, "E103.0.0", {"start": v(9287, 250) * mm, "end": v(9287, -1120.1) * mm});
            skLineSegment(sketch, "E103.0.2", {"start": v(9287, -1120.1) * mm, "end": v(9287, 250) * mm, "construction": true});
            skPoint(sketch, "E104.orphan", {"position": v(6480.55, -1261.99) * mm});
            skPoint(sketch, "E105.orphan", {"position": v(17788.55, -738.69) * mm});
            skLineSegment(sketch, "E106.0.0", {"start": v(12114, 250) * mm, "end": v(12114, -989.28) * mm, "construction": true});
            skLineSegment(sketch, "E107.0.1", {"start": v(12104, -989.74) * mm, "end": v(12104, 250) * mm, "construction": true});
            skLineSegment(sketch, "E108", {"start": v(12104, -1001.75) * mm, "end": v(12104, -1539.67) * mm});
            skLineSegment(sketch, "E109", {"start": v(12114, -1001.29) * mm, "end": v(12114, -1539.2) * mm});
            skLineSegment(sketch, "E110.trimOffspring", {"start": v(12104, -1539.67) * mm, "end": v(12599.56, -1516.73) * mm});
            skSolve(sketch);
        }
        {
            var Q0;
            Q0=makeQuery(id+"F34.imprint","IMPRINT",FACE,{"disambiguationData":[TD([[makeQuery(id+"F34.imprint","IMPRINT",EDGE,{"derivedFrom":sQuery(id+"F34.wireOp",EDGE,"E97")}),-1.0]])]});
            var Q1;
            {var subQ0=sQuery(id+"F34.wireOp",EDGE,"E102");Q1=makeQuery(id+"F34.imprint","IMPRINT",FACE,{"disambiguationData":[TD([[makeQuery(id+"F34.imprint","IMPRINT",EDGE,{"derivedFrom":subQ0}),1.0]])]});}
            var Q2;
            {var subQ0=sQuery(id+"F34.wireOp",EDGE,"PiPcHzU6-lrqD-IbJk-a0se-360D3SzEsdvt");Q2=makeQuery(id+"F34.imprint","IMPRINT",FACE,{"disambiguationData":[TD([[makeQuery(id+"F34.imprint","IMPRINT",EDGE,{"derivedFrom":subQ0}),-1.0]])]});}
            extrude(context, id + "F35", {"entities" : qUnion([Q0, Q1, Q2]), "endBound" : BoundingType.SYMMETRIC, "depth" : 40 * mm});
        }
        {
            var Q0;
            {var subQ0=sQuery(id+"F34.wireOp",EDGE,"E108");Q0=makeQuery(id+"F34.imprint","IMPRINT",FACE,{"disambiguationData":[TD([[makeQuery(id+"F34.imprint","IMPRINT",EDGE,{"derivedFrom":subQ0}),1.0]])]});}
            var Q1;
            Q1=makeQuery(id+"F34.imprint","IMPRINT",FACE,{"disambiguationData":[TD([[makeQuery(id+"F34.imprint","IMPRINT",EDGE,{"derivedFrom":sQuery(id+"F34.wireOp",EDGE,"147c0c08-3ff6-4e21-8d80-8c8b1cdad619.0")}),1.0]])]});
            var Q2;
            Q2=makeQuery(id+"F16.opExtrude","SWEPT_FACE",FACE,{"disambiguationData":[OSD([sQuery(id+"F9.wireOp",EDGE,"E29")])]});
            extrude(context, id + "F36", {"entities" : qUnion([Q0, Q1]), "endBound" : BoundingType.UP_TO_SURFACE, "endBoundEntityFace" : qUnion([Q2]), "depth" : 25 * mm});
        }
        {
            var Q0;
            Q0=makeQuery(id+"F4.opExtrude","SWEPT_FACE",FACE,{"disambiguationData":[OSD([sQuery(id+"F1.wireOp",EDGE,"E22")])]});
            var sketch = newSketch(context, id + "F37", { "sketchPlane" : qUnion([Q0])});
            skLineSegment(sketch, "E111.0", {"start": v(1202, -6480) * mm, "end": v(1192, -6480) * mm});
            skLineSegment(sketch, "E112.0", {"start": v(890, -12114) * mm, "end": v(890, -12599.56) * mm});
            skLineSegment(sketch, "E113.0", {"start": v(930, -12114) * mm, "end": v(930, -12599.56) * mm});
            skLineSegment(sketch, "E114.0", {"start": v(930, -12104) * mm, "end": v(890, -12104) * mm});
            skLineSegment(sketch, "E115", {"start": v(890, -12114) * mm, "end": v(890, -12104) * mm});
            skLineSegment(sketch, "E116", {"start": v(930, -12114) * mm, "end": v(930, -12104) * mm});
            skPoint(sketch, "E117.orphan", {"position": v(937.79, -12104) * mm});
            skLineSegment(sketch, "E118", {"start": v(890, -12104) * mm, "end": v(1192, -6480) * mm});
            skLineSegment(sketch, "E119", {"start": v(930, -12104) * mm, "end": v(1235.6, -6412.78) * mm});
            skLineSegment(sketch, "E120.0", {"start": v(1202, -6480) * mm, "end": v(1235.6, -6412.78) * mm});
            skPoint(sketch, "E121.orphan", {"position": v(1262, -6360) * mm});
            skSolve(sketch);
        }
        {
            var Q0;
            Q0=makeQuery(id+"F37.imprint","IMPRINT",FACE,{"disambiguationData":[TD([[makeQuery(id+"F37.imprint","IMPRINT",EDGE,{"derivedFrom":sQuery(id+"F37.wireOp",EDGE,"E111.0")}),1.0]])]});
            var Q1;
            Q1=makeQuery(id+"F20.opExtrude","CAP_FACE",FACE,{"disambiguationData":[OSD([sQuery(id+"F19.wireOp",EDGE,"E47"),sQuery(id+"F19.wireOp",EDGE,"E48"),sQuery(id+"F19.wireOp",EDGE,"E49"),sQuery(id+"F19.wireOp",EDGE,"E50")])],"isStart":false});
            extrude(context, id + "F38", {"entities" : qUnion([Q0]), "endBound" : BoundingType.UP_TO_SURFACE, "oppositeDirection" : true, "endBoundEntityFace" : qUnion([Q1]), "depth" : 25 * mm});
        }
        {
            var Q0;
            Q0=makeQuery(id+"F35.opExtrude","CAP_FACE",FACE,{"disambiguationData":[OSD([sQuery(id+"F34.wireOp",EDGE,"E97"),sQuery(id+"F34.wireOp",EDGE,"E98"),sQuery(id+"F34.wireOp",EDGE,"E100.0"),sQuery(id+"F34.wireOp",EDGE,"E102"),sQuery(id+"F34.wireOp",EDGE,"E109"),sQuery(id+"F34.wireOp",EDGE,"E110.trimOffspring")])],"isStart":true});
            var sketch = newSketch(context, id + "F39", { "sketchPlane" : qUnion([Q0])});
            skPoint(sketch, "E122.0", {"position": v(-12104, -1539.67) * mm});
            skPoint(sketch, "E123.0", {"position": v(-6480, -1700) * mm});
            skLineSegment(sketch, "E124", {"start": v(-6480, -1700) * mm, "end": v(-12104, -1539.67) * mm});
            skLineSegment(sketch, "E125", {"start": v(-12104, -1539.67) * mm, "end": v(-12404.7, -1982.05) * mm});
            skLineSegment(sketch, "E126", {"start": v(-12404.7, -1982.05) * mm, "end": v(-6130.68, -2155.68) * mm});
            skLineSegment(sketch, "E127", {"start": v(-6130.68, -2155.68) * mm, "end": v(-6480, -1700) * mm});
            skSolve(sketch);
        }
        {
            var Q0;
            Q0=makeQuery(id+"F39.imprint","IMPRINT",FACE,{"disambiguationData":[TD([[makeQuery(id+"F39.imprint","IMPRINT",EDGE,{"derivedFrom":sQuery(id+"F39.wireOp",EDGE,"E124")}),1.0]])]});
            var Q1;
            Q1=makeQuery(id+"F4.opExtrude","CAP_FACE",FACE,{"disambiguationData":[OSD([sQuery(id+"F1.wireOp",EDGE,"E3"),sQuery(id+"F1.wireOp",EDGE,"E5"),sQuery(id+"F1.wireOp",EDGE,"E7"),sQuery(id+"F1.wireOp",EDGE,"E10"),sQuery(id+"F1.wireOp",EDGE,"E11"),sQuery(id+"F1.wireOp",EDGE,"E12"),sQuery(id+"F1.wireOp",EDGE,"E21"),sQuery(id+"F1.wireOp",EDGE,"E22")])],"isStart":false});
            extrude(context, id + "F40", {"entities" : qUnion([Q0]), "operationType" : NewBodyOperationType.REMOVE, "endBound" : BoundingType.UP_TO_SURFACE, "oppositeDirection" : true, "endBoundEntityFace" : qUnion([Q1]), "depth" : 25 * mm});
        }
        {
            var Q0;
            Q0=makeQuery(id+"F36.opExtrude","SWEPT_BODY",BODY,{"disambiguationData":[OSD([sQuery(id+"F34.wireOp",EDGE,"E100.0"),sQuery(id+"F34.wireOp",EDGE,"wkCY3c1k-fEoE-qsbi-krR3-03lMSVA7ufSa"),sQuery(id+"F34.wireOp",EDGE,"147c0c08-3ff6-4e21-8d80-8c8b1cdad619.0"),sQuery(id+"F34.wireOp",EDGE,"IWkWiKJU-Gfeq-o61c-AkVB-herKOvPIKmk6"),sQuery(id+"F34.wireOp",EDGE,"bdxZtwMk-0dta-mVQB-1oRu-CJuhaaxSo7uL"),sQuery(id+"F34.wireOp",EDGE,"E108"),sQuery(id+"F34.wireOp",EDGE,"E109")])]});
            var Q1;
            Q1=qCreatedBy(id+"F33.planeOp",FACE);
            mirror(context, id + "F41", {"operationType" : NewBodyOperationType.ADD, "entities" : qUnion([Q0]), "mirrorPlane" : qUnion([Q1])});
        }
        {
            var Q0;
            Q0=makeQuery(id+"F2.opExtrude","SWEPT_BODY",BODY,{"disambiguationData":[OSD([sQuery(id+"F1.wireOp",EDGE,"E0"),sQuery(id+"F1.wireOp",EDGE,"E4"),sQuery(id+"F1.wireOp",EDGE,"E6"),sQuery(id+"F1.wireOp",EDGE,"E9"),sQuery(id+"F1.wireOp",EDGE,"E15")])]});
            var Q1;
            Q1=makeQuery(id+"F4.opExtrude","SWEPT_BODY",BODY,{"disambiguationData":[OSD([sQuery(id+"F1.wireOp",EDGE,"E3"),sQuery(id+"F1.wireOp",EDGE,"E5"),sQuery(id+"F1.wireOp",EDGE,"E7"),sQuery(id+"F1.wireOp",EDGE,"E10"),sQuery(id+"F1.wireOp",EDGE,"E11"),sQuery(id+"F1.wireOp",EDGE,"E12"),sQuery(id+"F1.wireOp",EDGE,"E21"),sQuery(id+"F1.wireOp",EDGE,"E22")])]});
            var Q2;
            Q2=makeQuery(id+"F6.opExtrude","SWEPT_BODY",BODY,{"disambiguationData":[OSD([sQuery(id+"F1.wireOp",EDGE,"E4"),sQuery(id+"F1.wireOp",EDGE,"E5"),sQuery(id+"F1.wireOp",EDGE,"E6"),sQuery(id+"F1.wireOp",EDGE,"E11"),sQuery(id+"F1.wireOp",EDGE,"E12"),sQuery(id+"F1.wireOp",EDGE,"E14")])]});
            var Q3;
            Q3=makeQuery(id+"F7.opExtrude","SWEPT_BODY",BODY,{"disambiguationData":[OSD([sQuery(id+"F1.wireOp",EDGE,"E0"),sQuery(id+"F1.wireOp",EDGE,"E4"),sQuery(id+"F1.wireOp",EDGE,"E6"),sQuery(id+"F1.wireOp",EDGE,"E9"),sQuery(id+"F1.wireOp",EDGE,"E14")])]});
            var Q4;
            Q4=makeQuery(id+"F10.opExtrude","SWEPT_BODY",BODY,{"disambiguationData":[OSD([sQuery(id+"F9.wireOp",EDGE,"E23"),sQuery(id+"F9.wireOp",EDGE,"E24"),sQuery(id+"F9.wireOp",EDGE,"E26"),sQuery(id+"F9.wireOp",EDGE,"E27"),sQuery(id+"F9.wireOp",EDGE,"E28"),sQuery(id+"F9.wireOp",EDGE,"E29")])]});
            var Q5;
            Q5=makeQuery(id+"F12.opExtrude","SWEPT_BODY",BODY,{"disambiguationData":[OSD([sQuery(id+"F11.wireOp",EDGE,"E33"),sQuery(id+"F11.wireOp",EDGE,"E34"),sQuery(id+"F11.wireOp",EDGE,"E35.0"),sQuery(id+"F11.wireOp",EDGE,"E36"),sQuery(id+"F11.wireOp",EDGE,"E37"),sQuery(id+"F11.wireOp",EDGE,"E38")])]});
            var Q6;
            Q6=makeQuery(id+"F16.opExtrude","SWEPT_BODY",BODY,{"disambiguationData":[OSD([sQuery(id+"F9.wireOp",EDGE,"E25"),sQuery(id+"F9.wireOp",EDGE,"E28"),sQuery(id+"F9.wireOp",EDGE,"E29"),sQuery(id+"F9.wireOp",EDGE,"E30")])]});
            var Q7;
            Q7=makeQuery(id+"F20.opExtrude","SWEPT_BODY",BODY,{"disambiguationData":[OSD([sQuery(id+"F19.wireOp",EDGE,"E47"),sQuery(id+"F19.wireOp",EDGE,"E48"),sQuery(id+"F19.wireOp",EDGE,"E49"),sQuery(id+"F19.wireOp",EDGE,"E50")])]});
            var Q8;
            Q8=makeQuery(id+"F22.opExtrude","SWEPT_BODY",BODY,{"disambiguationData":[OSD([sQuery(id+"F21.wireOp",EDGE,"E52"),sQuery(id+"F21.wireOp",EDGE,"E55"),sQuery(id+"F21.wireOp",EDGE,"E56"),sQuery(id+"F21.wireOp",EDGE,"E57"),sQuery(id+"F21.wireOp",EDGE,"E58.0")])]});
            var Q9;
            Q9=makeQuery(id+"F13.opExtrude","SWEPT_BODY",BODY,{"disambiguationData":[OSD([sQuery(id+"F11.wireOp",EDGE,"E39.bottom"),sQuery(id+"F11.wireOp",EDGE,"E39.top"),sQuery(id+"F11.wireOp",EDGE,"E39.left"),sQuery(id+"F11.wireOp",EDGE,"E39.right")])]});
            var Q10;
            Q10=makeQuery(id+"F26.opBoolean","SPLIT",BODY,{"disambiguationData":[OD(0.0)],"derivedFrom":makeQuery(id+"F25.opExtrude","SWEPT_BODY",BODY,{"disambiguationData":[OSD([sQuery(id+"F24.wireOp",EDGE,"E71.bottom"),sQuery(id+"F24.wireOp",EDGE,"E71.top"),sQuery(id+"F24.wireOp",EDGE,"E71.left"),sQuery(id+"F24.wireOp",EDGE,"E71.right")])]})});
            var Q11;
            Q11=makeQuery(id+"F26.opBoolean","SPLIT",BODY,{"disambiguationData":[OD(0.0)],"derivedFrom":makeQuery(id+"F25.opExtrude","SWEPT_BODY",BODY,{"disambiguationData":[OSD([sQuery(id+"F24.wireOp",EDGE,"E72.bottom"),sQuery(id+"F24.wireOp",EDGE,"E72.top"),sQuery(id+"F24.wireOp",EDGE,"E72.left"),sQuery(id+"F24.wireOp",EDGE,"E72.right")])]})});
            var Q12;
            Q12=makeQuery(id+"F26.opBoolean","SPLIT",BODY,{"disambiguationData":[OD(0.0)],"derivedFrom":makeQuery(id+"F25.opExtrude","SWEPT_BODY",BODY,{"disambiguationData":[OSD([sQuery(id+"F24.wireOp",EDGE,"E73.bottom"),sQuery(id+"F24.wireOp",EDGE,"E73.top"),sQuery(id+"F24.wireOp",EDGE,"E73.left"),sQuery(id+"F24.wireOp",EDGE,"E73.right")])]})});
            var Q13;
            Q13=makeQuery(id+"F26.opBoolean","SPLIT",BODY,{"disambiguationData":[OD(0.0)],"derivedFrom":makeQuery(id+"F25.opExtrude","SWEPT_BODY",BODY,{"disambiguationData":[OSD([sQuery(id+"F24.wireOp",EDGE,"E75.bottom"),sQuery(id+"F24.wireOp",EDGE,"E75.top"),sQuery(id+"F24.wireOp",EDGE,"E75.left"),sQuery(id+"F24.wireOp",EDGE,"E75.right")])]})});
            var Q14;
            Q14=makeQuery(id+"F26.opBoolean","SPLIT",BODY,{"disambiguationData":[OD(0.0)],"derivedFrom":makeQuery(id+"F25.opExtrude","SWEPT_BODY",BODY,{"disambiguationData":[OSD([sQuery(id+"F24.wireOp",EDGE,"E74.bottom"),sQuery(id+"F24.wireOp",EDGE,"E74.top"),sQuery(id+"F24.wireOp",EDGE,"E74.left"),sQuery(id+"F24.wireOp",EDGE,"E74.right")])]})});
            var Q15;
            Q15=makeQuery(id+"F26.opBoolean","SPLIT",BODY,{"disambiguationData":[OD(0.0)],"derivedFrom":makeQuery(id+"F25.opExtrude","SWEPT_BODY",BODY,{"disambiguationData":[OSD([sQuery(id+"F24.wireOp",EDGE,"E76.bottom"),sQuery(id+"F24.wireOp",EDGE,"E76.top"),sQuery(id+"F24.wireOp",EDGE,"E76.left"),sQuery(id+"F24.wireOp",EDGE,"E76.right")])]})});
            var Q16;
            Q16=makeQuery(id+"F26.opBoolean","SPLIT",BODY,{"disambiguationData":[OD(0.0)],"derivedFrom":makeQuery(id+"F25.opExtrude","SWEPT_BODY",BODY,{"disambiguationData":[OSD([sQuery(id+"F24.wireOp",EDGE,"E77.bottom"),sQuery(id+"F24.wireOp",EDGE,"E77.top"),sQuery(id+"F24.wireOp",EDGE,"E77.left"),sQuery(id+"F24.wireOp",EDGE,"E77.right")])]})});
            var Q17;
            Q17=makeQuery(id+"F26.opBoolean","SPLIT",BODY,{"disambiguationData":[OD(0.0)],"derivedFrom":makeQuery(id+"F25.opExtrude","SWEPT_BODY",BODY,{"disambiguationData":[OSD([sQuery(id+"F24.wireOp",EDGE,"E78.bottom"),sQuery(id+"F24.wireOp",EDGE,"E78.top"),sQuery(id+"F24.wireOp",EDGE,"E78.left"),sQuery(id+"F24.wireOp",EDGE,"E78.right")])]})});
            var Q18;
            Q18=makeQuery(id+"F26.opBoolean","SPLIT",BODY,{"disambiguationData":[OD(1.0)],"derivedFrom":makeQuery(id+"F25.opExtrude","SWEPT_BODY",BODY,{"disambiguationData":[OSD([sQuery(id+"F24.wireOp",EDGE,"E68.bottom"),sQuery(id+"F24.wireOp",EDGE,"E68.top"),sQuery(id+"F24.wireOp",EDGE,"E68.left"),sQuery(id+"F24.wireOp",EDGE,"E68.right")])]})});
            var Q19;
            Q19=makeQuery(id+"F32.opExtrude","SWEPT_BODY",BODY,{"disambiguationData":[OSD([sQuery(id+"F29.wireOp",EDGE,"E83"),sQuery(id+"F29.wireOp",EDGE,"E85.0"),sQuery(id+"F29.wireOp",EDGE,"E87"),sQuery(id+"F29.wireOp",EDGE,"E88.0"),sQuery(id+"F29.wireOp",EDGE,"E89")])]});
            var Q20;
            Q20=makeQuery(id+"F32.opExtrude","SWEPT_BODY",BODY,{"disambiguationData":[OSD([sQuery(id+"F29.wireOp",EDGE,"E84"),sQuery(id+"F29.wireOp",EDGE,"E90.0"),sQuery(id+"F29.wireOp",EDGE,"E91"),sQuery(id+"F29.wireOp",EDGE,"E92.0.3"),sQuery(id+"F29.wireOp",EDGE,"E93")])]});
            var Q21;
            Q21=makeQuery(id+"F35.opExtrude","SWEPT_BODY",BODY,{"disambiguationData":[OSD([sQuery(id+"F34.wireOp",EDGE,"E97"),sQuery(id+"F34.wireOp",EDGE,"E98"),sQuery(id+"F34.wireOp",EDGE,"E100.0"),sQuery(id+"F34.wireOp",EDGE,"E102"),sQuery(id+"F34.wireOp",EDGE,"E109"),sQuery(id+"F34.wireOp",EDGE,"E110.trimOffspring")])]});
            var Q22;
            Q22=makeQuery(id+"F36.opExtrude","SWEPT_BODY",BODY,{"disambiguationData":[OSD([sQuery(id+"F34.wireOp",EDGE,"E100.0"),sQuery(id+"F34.wireOp",EDGE,"E108"),sQuery(id+"F34.wireOp",EDGE,"E109"),sQuery(id+"F34.wireOp",EDGE,"E110.trimOffspring")])]});
            var Q23;
            Q23=makeQuery(id+"F30.opExtrude","SWEPT_BODY",BODY,{"disambiguationData":[OSD([sQuery(id+"F29.wireOp",EDGE,"E79"),sQuery(id+"F29.wireOp",EDGE,"E80"),sQuery(id+"F29.wireOp",EDGE,"E82.0"),sQuery(id+"F29.wireOp",EDGE,"E83"),sQuery(id+"F29.wireOp",EDGE,"E84")])]});
            var Q24;
            Q24=makeQuery(id+"F38.opExtrude","SWEPT_BODY",BODY,{"disambiguationData":[OSD([sQuery(id+"F37.wireOp",EDGE,"E111.0"),sQuery(id+"F37.wireOp",EDGE,"E114.0"),sQuery(id+"F37.wireOp",EDGE,"E118"),sQuery(id+"F37.wireOp",EDGE,"E119"),sQuery(id+"F37.wireOp",EDGE,"E120.0")])]});
            var Q25;
            Q25=makeQuery(id+"F30.opExtrude","SWEPT_BODY",BODY,{"disambiguationData":[OSD([sQuery(id+"F29.wireOp",EDGE,"E85.0"),sQuery(id+"F29.wireOp",EDGE,"E94"),sQuery(id+"F29.wireOp",EDGE,"E95"),sQuery(id+"F29.wireOp",EDGE,"E96")])]});
            var Q26;
            Q26=qCreatedBy(makeId("Right.planeOp"),FACE);
            mirror(context, id + "F42", {"entities" : qUnion([Q0, Q1, Q2, Q3, Q4, Q5, Q6, Q7, Q8, Q9, Q10, Q11, Q12, Q13, Q14, Q15, Q16, Q17, Q18, Q19, Q20, Q21, Q22, Q23, Q24, Q25]), "mirrorPlane" : qUnion([Q26])});
        }
        {
            var Q0;
            Q0=makeQuery(id+"F2.opExtrude","CAP_FACE",FACE,{"disambiguationData":[OSD([sQuery(id+"F1.wireOp",EDGE,"E0"),sQuery(id+"F1.wireOp",EDGE,"E4"),sQuery(id+"F1.wireOp",EDGE,"E6"),sQuery(id+"F1.wireOp",EDGE,"E9"),sQuery(id+"F1.wireOp",EDGE,"E15")])],"isStart":false});
            var sketch = newSketch(context, id + "F43", { "sketchPlane" : qUnion([Q0])});
            skCircle(sketch, "E128.0", {"center": v(0, 0) * mm, "radius": 80 * mm});
            skSolve(sketch);
        }
        {
            var Q0;
            Q0=makeQuery(id+"F43.imprint","IMPRINT",FACE,{"disambiguationData":[TD([[makeQuery(id+"F43.imprint","IMPRINT",EDGE,{"derivedFrom":sQuery(id+"F43.wireOp",EDGE,"E128.0")}),1.0]])]});
            var Q1;
            Q1=makeQuery(id+"F42.opPattern","COPY",FACE,{"derivedFrom":makeQuery(id+"F2.opExtrude","CAP_FACE",FACE,{"disambiguationData":[OSD([sQuery(id+"F1.wireOp",EDGE,"E0"),sQuery(id+"F1.wireOp",EDGE,"E4"),sQuery(id+"F1.wireOp",EDGE,"E6"),sQuery(id+"F1.wireOp",EDGE,"E9"),sQuery(id+"F1.wireOp",EDGE,"E15")])],"isStart":false}),"instanceName":"1"});
            extrude(context, id + "F44", {"entities" : qUnion([Q0]), "endBound" : BoundingType.UP_TO_SURFACE, "oppositeDirection" : true, "endBoundEntityFace" : qUnion([Q1]), "depth" : 25 * mm});
        }
        {
            var Q0;
            Q0=makeQuery(id+"F4.opExtrude","CAP_FACE",FACE,{"disambiguationData":[OSD([sQuery(id+"F1.wireOp",EDGE,"E3"),sQuery(id+"F1.wireOp",EDGE,"E5"),sQuery(id+"F1.wireOp",EDGE,"E7"),sQuery(id+"F1.wireOp",EDGE,"E8"),sQuery(id+"F1.wireOp",EDGE,"E10"),sQuery(id+"F1.wireOp",EDGE,"E11"),sQuery(id+"F1.wireOp",EDGE,"E12")])],"isStart":false});
            var sketch = newSketch(context, id + "F45", { "sketchPlane" : qUnion([Q0])});
            skCircle(sketch, "E129.0", {"center": v(5800, -1450) * mm, "radius": 105 * mm});
            skSolve(sketch);
        }
        {
            var Q0;
            Q0=makeQuery(id+"F45.imprint","IMPRINT",FACE,{"disambiguationData":[TD([[makeQuery(id+"F45.imprint","IMPRINT",EDGE,{"derivedFrom":sQuery(id+"F45.wireOp",EDGE,"E129.0")}),1.0]])]});
            var Q1;
            Q1=makeQuery(id+"F42.opPattern","COPY",FACE,{"derivedFrom":makeQuery(id+"F4.opExtrude","CAP_FACE",FACE,{"disambiguationData":[OSD([sQuery(id+"F1.wireOp",EDGE,"E3"),sQuery(id+"F1.wireOp",EDGE,"E5"),sQuery(id+"F1.wireOp",EDGE,"E7"),sQuery(id+"F1.wireOp",EDGE,"E8"),sQuery(id+"F1.wireOp",EDGE,"E10"),sQuery(id+"F1.wireOp",EDGE,"E11"),sQuery(id+"F1.wireOp",EDGE,"E12")])],"isStart":false}),"instanceName":"1"});
            extrude(context, id + "F46", {"entities" : qUnion([Q0]), "oppositeDirection" : true, "endBoundEntityFace" : qUnion([Q1]), "offsetDistance" : 25 * mm, "depth" : (35 + (35 + 50)) * mm, "hasSecondDirection" : true, "secondDirectionOppositeDirection" : true, "secondDirectionDepth" : (35 - (35 + 50)) * mm});
        }
        {
            var Q0;
            Q0=makeQuery(id+"F35.opExtrude","CAP_FACE",FACE,{"disambiguationData":[OSD([sQuery(id+"F34.wireOp",EDGE,"E97"),sQuery(id+"F34.wireOp",EDGE,"E98"),sQuery(id+"F34.wireOp",EDGE,"E100.0"),sQuery(id+"F34.wireOp",EDGE,"E102"),sQuery(id+"F34.wireOp",EDGE,"wkCY3c1k-fEoE-qsbi-krR3-03lMSVA7ufSa"),sQuery(id+"F34.wireOp",EDGE,"E109")])],"isStart":false});
            var sketch = newSketch(context, id + "F47", { "sketchPlane" : qUnion([Q0])});
            skCircle(sketch, "E130.0", {"center": v(12588, -1267) * mm, "radius": 70 * mm});
            skSolve(sketch);
        }
        {
            var Q0;
            Q0=makeQuery(id+"F47.imprint","IMPRINT",FACE,{"disambiguationData":[TD([[makeQuery(id+"F47.imprint","IMPRINT",EDGE,{"derivedFrom":sQuery(id+"F47.wireOp",EDGE,"E130.0")}),1.0]])]});
            var Q1;
            Q1=makeQuery(id+"F42.opPattern","COPY",FACE,{"derivedFrom":makeQuery(id+"F35.opExtrude","CAP_FACE",FACE,{"disambiguationData":[OSD([sQuery(id+"F34.wireOp",EDGE,"E97"),sQuery(id+"F34.wireOp",EDGE,"E98"),sQuery(id+"F34.wireOp",EDGE,"E100.0"),sQuery(id+"F34.wireOp",EDGE,"E102"),sQuery(id+"F34.wireOp",EDGE,"wkCY3c1k-fEoE-qsbi-krR3-03lMSVA7ufSa"),sQuery(id+"F34.wireOp",EDGE,"E109")])],"isStart":false}),"instanceName":"1"});
            extrude(context, id + "F48", {"entities" : qUnion([Q0]), "oppositeDirection" : true, "endBoundEntityFace" : qUnion([Q1]), "offsetDistance" : 25 * mm, "depth" : 330 * mm});
        }
    });
